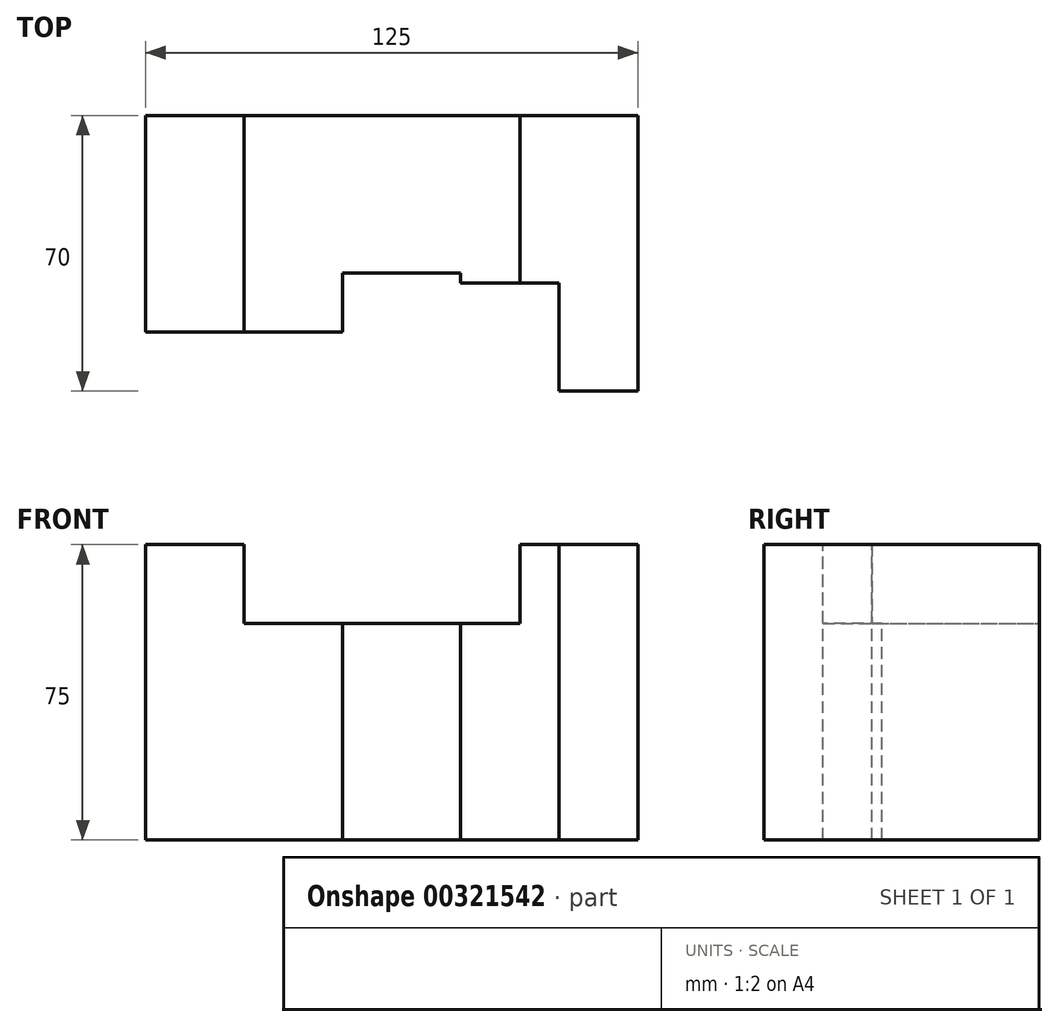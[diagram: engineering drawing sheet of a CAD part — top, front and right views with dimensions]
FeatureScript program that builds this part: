
annotation { "Feature Type Name" : "Feature", "Feature Type Description" : "" }
export const myFeature = defineFeature(function(context is Context, id is Id, definition is map)
    precondition{}
    {
        {
            var Q0;
            Q0=qCreatedBy(makeId("Front.planeOp"),FACE);
            var sketch = newSketch(context, id + "F0", { "sketchPlane" : qUnion([Q0])});
            skLineSegment(sketch, "E0", {"start": v(0, 0) * mm, "end": v(0, 75) * mm});
            skLineSegment(sketch, "E1", {"start": v(0, 75) * mm, "end": v(25, 75) * mm});
            skLineSegment(sketch, "E2", {"start": v(25, 75) * mm, "end": v(25, 55) * mm});
            skLineSegment(sketch, "E3", {"start": v(25, 55) * mm, "end": v(95, 55) * mm});
            skLineSegment(sketch, "E4", {"start": v(95, 55) * mm, "end": v(95, 75) * mm});
            skLineSegment(sketch, "E5", {"start": v(95, 75) * mm, "end": v(125, 75) * mm});
            skLineSegment(sketch, "E6", {"start": v(125, 75) * mm, "end": v(125, 0) * mm});
            skLineSegment(sketch, "E7", {"start": v(125, 0) * mm, "end": v(0, 0) * mm});
            skSolve(sketch);
        }
        {
            var Q0;
            Q0=makeQuery(id+"F0.imprint","IMPRINT",FACE,{"disambiguationData":[TD([[makeQuery(id+"F0.imprint","IMPRINT",EDGE,{"derivedFrom":sQuery(id+"F0.wireOp",EDGE,"E0")}),-1.0]])]});
            extrude(context, id + "F1", {"entities" : qUnion([Q0]), "depth" : 70 * mm});
        }
        {
            var Q0;
            Q0=qCreatedBy(makeId("Top.planeOp"),FACE);
            cPlane(context, id + "F2", {"entities" : qUnion([Q0]), "cplaneType" : CPlaneType.OFFSET, "offset" : 75 * mm, "width" : 150 * mm, "height" : 150 * mm});
        }
        {
            var Q0;
            Q0=qCreatedBy(id+"F2.planeOp",FACE);
            var sketch = newSketch(context, id + "F3", { "sketchPlane" : qUnion([Q0])});
            skLineSegment(sketch, "E8", {"start": v(0, 0) * mm, "end": v(125, 0) * mm});
            skLineSegment(sketch, "E9", {"start": v(125, 0) * mm, "end": v(125, -70) * mm});
            skLineSegment(sketch, "E10", {"start": v(125, -70) * mm, "end": v(0, -70) * mm});
            skLineSegment(sketch, "E11", {"start": v(0, -70) * mm, "end": v(0, 0) * mm});
            skLineSegment(sketch, "E12", {"start": v(125, -70) * mm, "end": v(105, -70) * mm});
            skLineSegment(sketch, "E13", {"start": v(105, -70) * mm, "end": v(105, -42.5) * mm});
            skLineSegment(sketch, "E14", {"start": v(105, -42.5) * mm, "end": v(80, -42.5) * mm});
            skLineSegment(sketch, "E15", {"start": v(80, -42.5) * mm, "end": v(80, -40) * mm});
            skLineSegment(sketch, "E16", {"start": v(80, -40) * mm, "end": v(50, -40) * mm});
            skLineSegment(sketch, "E17", {"start": v(50, -40) * mm, "end": v(50, -55) * mm});
            skLineSegment(sketch, "E18", {"start": v(50, -55) * mm, "end": v(0, -55) * mm});
            skLineSegment(sketch, "E19", {"start": v(0, -55) * mm, "end": v(0, 0) * mm});
            skSolve(sketch);
        }
        {
            var Q0;
            Q0=makeQuery(id+"F3.imprint","IMPRINT",FACE,{"disambiguationData":[TD([[makeQuery(id+"F3.imprint","IMPRINT",EDGE,{"derivedFrom":sQuery(id+"F3.wireOp",EDGE,"E10")}),-1.0]])]});
            extrude(context, id + "F4", {"entities" : qUnion([Q0]), "operationType" : NewBodyOperationType.REMOVE, "endBound" : BoundingType.THROUGH_ALL, "oppositeDirection" : true, "depth" : 25 * mm});
        }
    });
